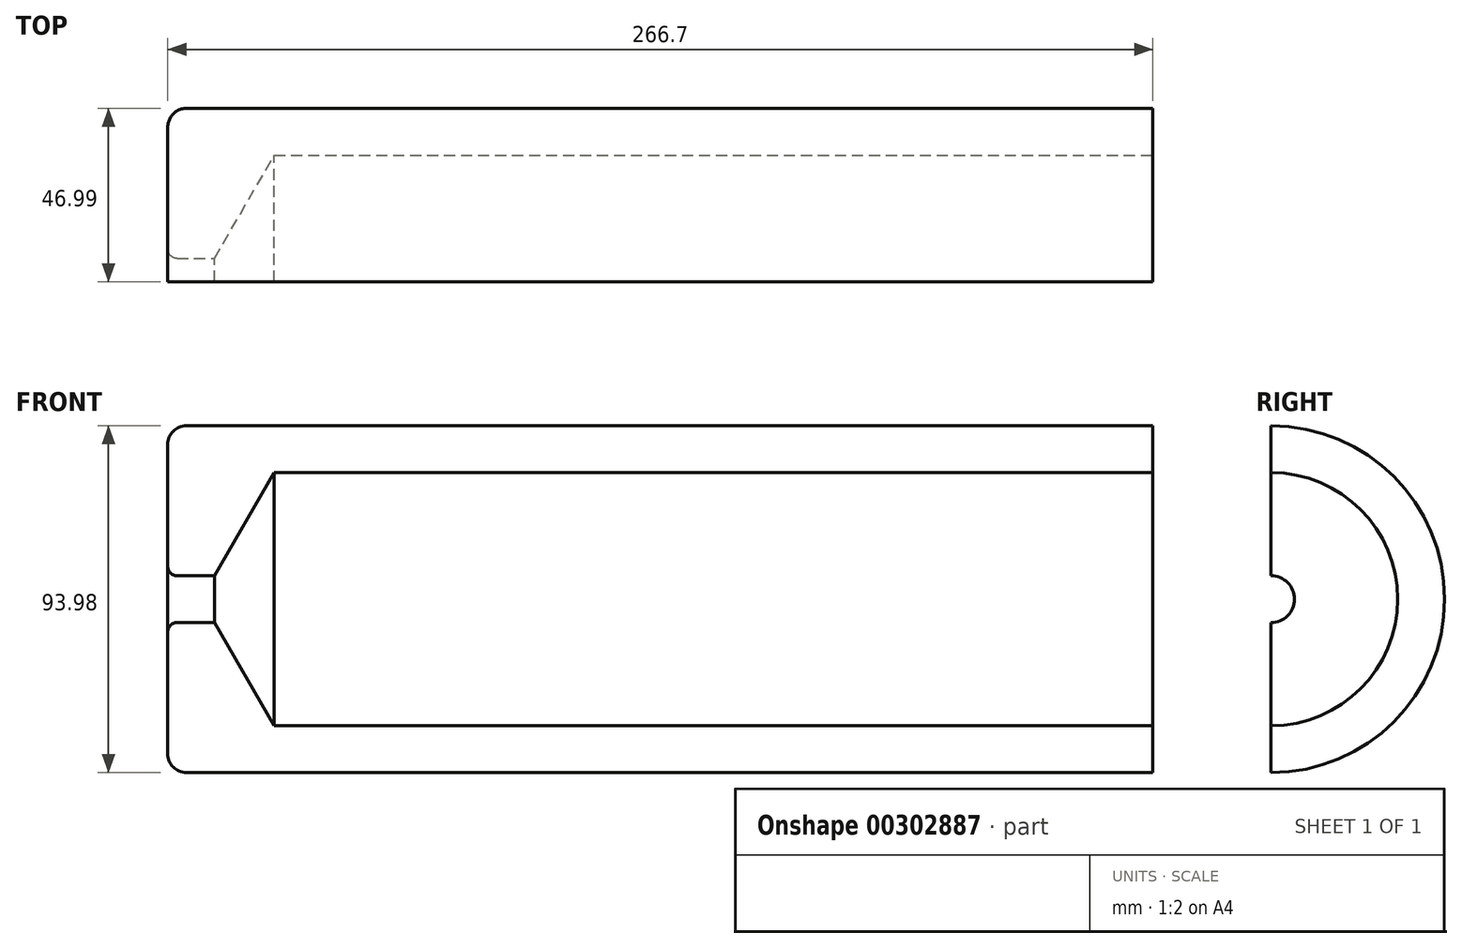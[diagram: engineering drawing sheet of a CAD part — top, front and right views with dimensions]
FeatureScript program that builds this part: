
annotation { "Feature Type Name" : "Feature", "Feature Type Description" : "" }
export const myFeature = defineFeature(function(context is Context, id is Id, definition is map)
    precondition{}
    {
        {
            var Q0;
            Q0=qCreatedBy(makeId("Front.planeOp"),FACE);
            var sketch = newSketch(context, id + "F0", { "sketchPlane" : qUnion([Q0])});
            skLineSegment(sketch, "E0", {"start": v(-133.35, 47) * mm, "end": v(133.35, 47) * mm});
            skLineSegment(sketch, "E1", {"start": v(-133.35, 46.99) * mm, "end": v(-133.35, 6.35) * mm});
            skLineSegment(sketch, "E2", {"start": v(-133.35, 6.35) * mm, "end": v(-120.65, 6.35) * mm});
            skLineSegment(sketch, "E3", {"start": v(-120.65, 6.35) * mm, "end": v(-104.52, 34.29) * mm});
            skLineSegment(sketch, "E4", {"start": v(-104.52, 34.3) * mm, "end": v(133.35, 34.3) * mm});
            skLineSegment(sketch, "E5", {"start": v(133.35, 34.3) * mm, "end": v(133.35, 47) * mm});
            skLineSegment(sketch, "E6", {"start": v(-120.65, 6.35) * mm, "end": v(-120.65, 25.91) * mm, "construction": true});
            skLineSegment(sketch, "E7", {"start": v(-155.63, 0) * mm, "end": v(157.8, 0) * mm, "construction": true});
            skSolve(sketch);
        }
        {
            var Q0;
            Q0 = qSketchRegion(id + "F0", true);
            var Q1;
            Q1=sQuery(id+"F0.wireOp",EDGE,"E7");
            revolve(context, id + "F1", {"entities" : qUnion([Q0]), "axis" : qUnion([Q1]), "revolveType" : RevolveType.ONE_DIRECTION, "oppositeDirection" : true, "angle" : 180 * degree});
        }
        {
            var Q0;
            Q0=makeQuery(id+"F1.opRevolve","SWEPT_EDGE",EDGE,{"disambiguationData":[OSD([sQuery(id+"F0.wireOp",EDGE,"E0"),sQuery(id+"F0.wireOp",EDGE,"E1")])]});
            fillet(context, id + "F2", {"entities" : qUnion([Q0]), "radius" : 5.08 * mm, "tangentPropagation" : true, "allowEdgeOverflow" : false});
        }
        {
            var Q0;
            Q0=makeQuery(id+"F1.opRevolve","SWEPT_EDGE",EDGE,{"disambiguationData":[OSD([sQuery(id+"F0.wireOp",EDGE,"E1"),sQuery(id+"F0.wireOp",EDGE,"E2")])]});
            fillet(context, id + "F3", {"entities" : qUnion([Q0]), "radius" : 2.54 * mm, "tangentPropagation" : true, "allowEdgeOverflow" : false});
        }
    });
